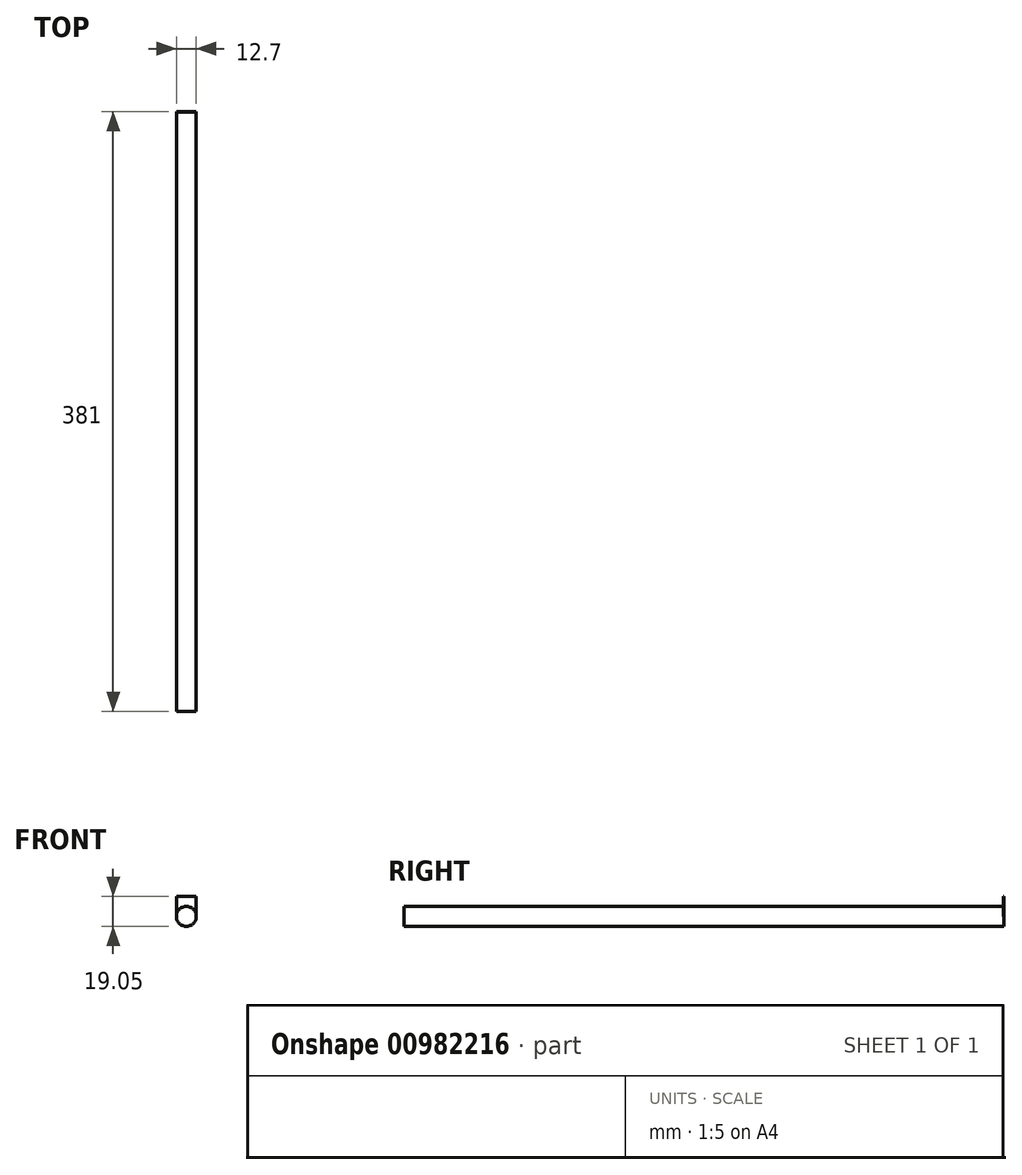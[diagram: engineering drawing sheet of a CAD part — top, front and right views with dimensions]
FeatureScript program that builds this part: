
annotation { "Feature Type Name" : "Feature", "Feature Type Description" : "" }
export const myFeature = defineFeature(function(context is Context, id is Id, definition is map)
    precondition{}
    {
        {
            var Q0;
            Q0=qCreatedBy(makeId("Front.planeOp"),FACE);
            var sketch = newSketch(context, id + "F0", { "sketchPlane" : qUnion([Q0])});
            skCircle(sketch, "E0", {"center": v(0, 0) * mm, "radius": 6.35 * mm});
            skSolve(sketch);
        }
        {
            var Q0;
            Q0=makeQuery(id+"F0.imprint","IMPRINT",FACE,{"disambiguationData":[TD([[makeQuery(id+"F0.imprint","IMPRINT",EDGE,{"derivedFrom":sQuery(id+"F0.wireOp",EDGE,"E0")}),1.0]])]});
            extrude(context, id + "F1", {"entities" : qUnion([Q0]), "depth" : 127 * mm, "offsetDistance" : 25.4 * mm});
        }
        {
            var Q0;
            Q0=makeQuery(id+"F1.opExtrude","CAP_FACE",FACE,{"disambiguationData":[OSD([sQuery(id+"F0.wireOp",EDGE,"E0")])],"isStart":true});
            extrude(context, id + "F2", {"entities" : qUnion([Q0]), "operationType" : NewBodyOperationType.ADD, "depth" : 254 * mm, "offsetDistance" : 25.4 * mm});
        }
        {
            var Q0;
            Q0=makeQuery(id+"F2.opExtrude","CAP_FACE",FACE,{"disambiguationData":[OSD([sQuery(id+"F0.wireOp",EDGE,"E0")])],"isStart":false});
            var sketch = newSketch(context, id + "F3", { "sketchPlane" : qUnion([Q0])});
            skLineSegment(sketch, "E1", {"start": v(0, 0) * mm, "end": v(-6.35, 0) * mm, "construction": true});
            skLineSegment(sketch, "E2", {"start": v(0, 0) * mm, "end": v(6.35, 0) * mm, "construction": true});
            skLineSegment(sketch, "E3.bottom", {"start": v(-6.35, 0) * mm, "end": v(6.35, 0) * mm, "construction": true});
            skLineSegment(sketch, "E3.top", {"start": v(-6.35, 12.7) * mm, "end": v(6.35, 12.7) * mm, "construction": true});
            skLineSegment(sketch, "E3.left", {"start": v(-6.35, 0) * mm, "end": v(-6.35, 12.7) * mm, "construction": true});
            skLineSegment(sketch, "E3.right", {"start": v(6.35, 0) * mm, "end": v(6.35, 12.7) * mm, "construction": true});
            skLineSegment(sketch, "E4", {"start": v(-6.35, 12.7) * mm, "end": v(6.35, 12.7) * mm});
            skLineSegment(sketch, "E5", {"start": v(6.35, 0) * mm, "end": v(-6.35, 0) * mm});
            skLineSegment(sketch, "E6", {"start": v(-6.35, 12.7) * mm, "end": v(-6.35, 0) * mm});
            skLineSegment(sketch, "E7", {"start": v(6.35, 12.7) * mm, "end": v(6.35, 0) * mm});
            skSolve(sketch);
        }
        {
            var Q0;
            Q0=makeQuery(id+"F3.imprint","IMPRINT",FACE,{"disambiguationData":[TD([[makeQuery(id+"F3.imprint","IMPRINT",EDGE,{"derivedFrom":sQuery(id+"F3.wireOp",EDGE,"E4")}),-1.0]])]});
            extrude(context, id + "F4", {"entities" : qUnion([Q0]), "operationType" : NewBodyOperationType.ADD, "oppositeDirection" : true, "depth" : 0.25 * mm, "offsetDistance" : 25.4 * mm});
        }
    });
